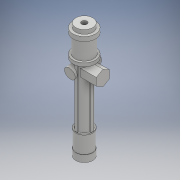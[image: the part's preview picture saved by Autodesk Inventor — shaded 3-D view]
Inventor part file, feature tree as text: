
AUTODESK INVENTOR PART (.ipt)
format: ipt  version: 2018 (Build 220112000, 112)  size: 287,232 bytes
history: native  units: mm
features: sketch x14, extrude x12, other x3, hole x2
ambient origin geometry x8: Origin, YZ Plane, XZ Plane, XY Plane, X Axis, Y Axis, Z Axis, Center Point
bodies: Body1 (feature_tree)
feature tree (31):
  extrude  "押し出し4"  Depth=50.0mm
  extrude  "押し出し5"  Depth=20.0mm TaperAngle=0.0deg
  extrude  "押し出し6"  Depth=48.0mm
  extrude  "押し出し7"  Depth=50.0mm TaperAngle=0.0deg
  extrude  "押し出し8"  Depth=50.0mm
  other  "作業平面4"
  extrude  "押し出し9"  Depth=3.0mm TaperAngle=0.0deg
  extrude  "押し出し10"  Depth=48.0mm
  extrude  "押し出し11"  Depth=42.0mm
  extrude  "押し出し12"  Depth=130.0mm TaperAngle=0.0deg
  other  "作業平面6"
  extrude  "押し出し13"  Depth=55.0mm TaperAngle=0.0deg
  extrude  "押し出し14"  Depth=187.0mm
  hole  "穴1"  [1 undecoded]
  extrude  "押し出し15"  Depth=54.0mm TaperAngle=0.0deg
  hole  "穴2"  [1 undecoded]
  sketch  "スケッチ5"
  sketch  "スケッチ6"
  sketch  "スケッチ7"
  sketch  "スケッチ8"
  sketch  "スケッチ11"
  sketch  "スケッチ12"
  sketch  "スケッチ13"
  sketch  "スケッチ14"
  sketch  "スケッチ15"
  other  "作業平面5"
  sketch  "スケッチ16"
  sketch  "スケッチ17"
  sketch  "スケッチ18"
  sketch  "スケッチ19"
  sketch  "スケッチ20"
note: 2 required parameter values undecoded (feature->parameter linkage not recoverable at this tier; creation-order binding heuristic only, values carry confidence <= 0.55)
